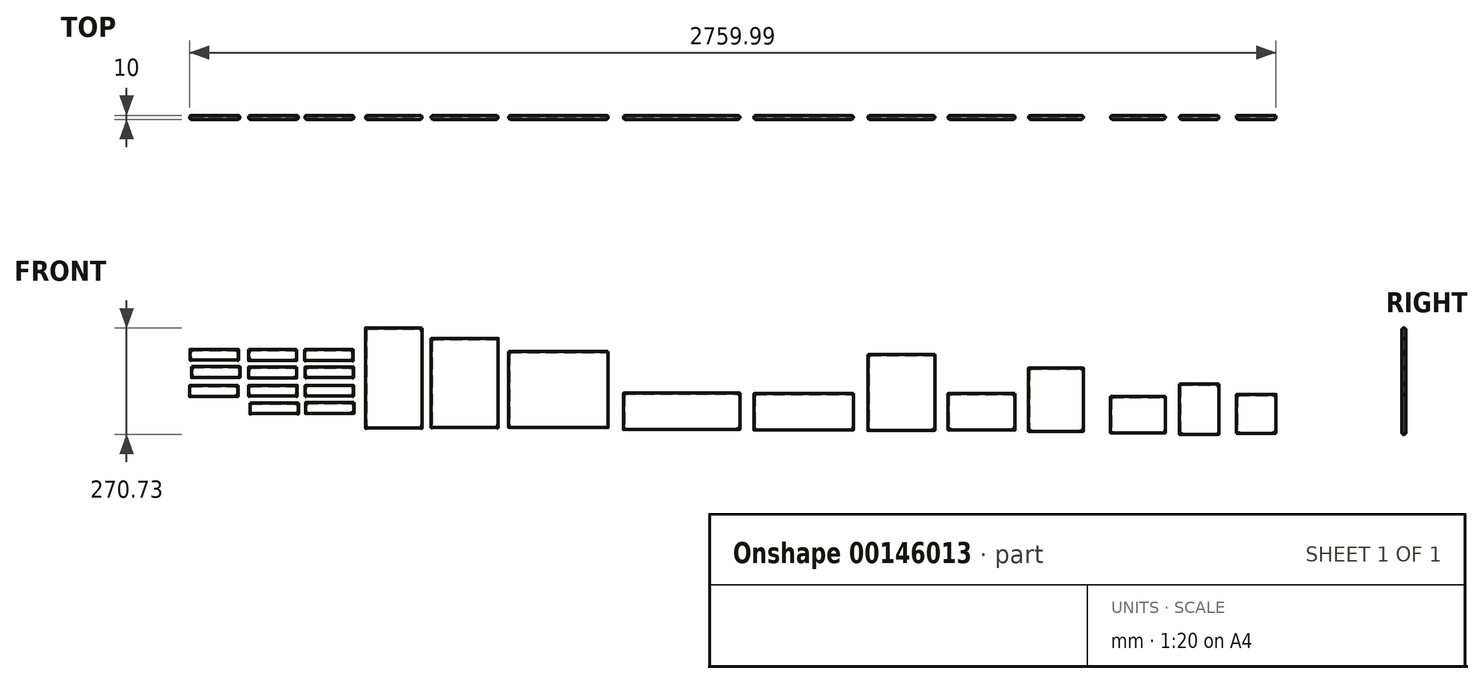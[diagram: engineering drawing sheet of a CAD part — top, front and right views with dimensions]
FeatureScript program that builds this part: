
annotation { "Feature Type Name" : "Feature", "Feature Type Description" : "" }
export const myFeature = defineFeature(function(context is Context, id is Id, definition is map)
    precondition{}
    {
        {
            var Q0;
            Q0=qCreatedBy(makeId("Front.planeOp"),FACE);
            var sketch = newSketch(context, id + "F0", { "sketchPlane" : qUnion([Q0])});
            skLineSegment(sketch, "E0.bottom", {"start": v(-185.42, 51.02) * mm, "end": v(-62.42, 51.02) * mm});
            skLineSegment(sketch, "E0.top", {"start": v(-185.42, 79.02) * mm, "end": v(-62.42, 79.02) * mm});
            skLineSegment(sketch, "E0.left", {"start": v(-185.42, 51.02) * mm, "end": v(-185.42, 79.02) * mm});
            skLineSegment(sketch, "E0.right", {"start": v(-62.42, 51.02) * mm, "end": v(-62.42, 79.02) * mm});
            skLineSegment(sketch, "E1.bottom", {"start": v(-184.61, -39.22) * mm, "end": v(-61.61, -39.22) * mm});
            skLineSegment(sketch, "E1.top", {"start": v(-184.61, -11.22) * mm, "end": v(-61.61, -11.22) * mm});
            skLineSegment(sketch, "E1.left", {"start": v(-184.61, -39.22) * mm, "end": v(-184.61, -11.22) * mm});
            skLineSegment(sketch, "E1.right", {"start": v(-61.61, -39.22) * mm, "end": v(-61.61, -11.22) * mm});
            skLineSegment(sketch, "E2.bottom", {"start": v(-183.78, -83.5) * mm, "end": v(-60.78, -83.5) * mm});
            skLineSegment(sketch, "E2.top", {"start": v(-183.78, -55.5) * mm, "end": v(-60.78, -55.5) * mm});
            skLineSegment(sketch, "E2.left", {"start": v(-183.78, -83.5) * mm, "end": v(-183.78, -55.5) * mm});
            skLineSegment(sketch, "E2.right", {"start": v(-60.78, -83.5) * mm, "end": v(-60.78, -55.5) * mm});
            skLineSegment(sketch, "E3.bottom", {"start": v(-328.72, 51.62) * mm, "end": v(-205.72, 51.62) * mm});
            skLineSegment(sketch, "E3.top", {"start": v(-328.72, 79.62) * mm, "end": v(-205.72, 79.62) * mm});
            skLineSegment(sketch, "E3.left", {"start": v(-328.72, 51.62) * mm, "end": v(-328.72, 79.62) * mm});
            skLineSegment(sketch, "E3.right", {"start": v(-205.72, 51.62) * mm, "end": v(-205.72, 79.62) * mm});
            skLineSegment(sketch, "E4.bottom", {"start": v(-184.79, 7.45) * mm, "end": v(-61.79, 7.45) * mm});
            skLineSegment(sketch, "E4.top", {"start": v(-184.79, 35.45) * mm, "end": v(-61.79, 35.45) * mm});
            skLineSegment(sketch, "E4.left", {"start": v(-184.79, 7.45) * mm, "end": v(-184.79, 35.45) * mm});
            skLineSegment(sketch, "E4.right", {"start": v(-61.79, 7.45) * mm, "end": v(-61.79, 35.45) * mm});
            skLineSegment(sketch, "E5.bottom", {"start": v(-328.7, 6.95) * mm, "end": v(-205.7, 6.95) * mm});
            skLineSegment(sketch, "E5.top", {"start": v(-328.7, 34.95) * mm, "end": v(-205.7, 34.95) * mm});
            skLineSegment(sketch, "E5.left", {"start": v(-328.7, 6.95) * mm, "end": v(-328.7, 34.95) * mm});
            skLineSegment(sketch, "E5.right", {"start": v(-205.7, 6.95) * mm, "end": v(-205.7, 34.95) * mm});
            skLineSegment(sketch, "E6.bottom", {"start": v(-477.03, 51.95) * mm, "end": v(-354.03, 51.95) * mm});
            skLineSegment(sketch, "E6.top", {"start": v(-477.03, 79.95) * mm, "end": v(-354.03, 79.95) * mm});
            skLineSegment(sketch, "E6.left", {"start": v(-477.03, 51.95) * mm, "end": v(-477.03, 79.95) * mm});
            skLineSegment(sketch, "E6.right", {"start": v(-354.03, 51.95) * mm, "end": v(-354.03, 79.95) * mm});
            skLineSegment(sketch, "E7.bottom", {"start": v(-473.24, 7.86) * mm, "end": v(-350.24, 7.86) * mm});
            skLineSegment(sketch, "E7.top", {"start": v(-473.24, 35.86) * mm, "end": v(-350.24, 35.86) * mm});
            skLineSegment(sketch, "E7.left", {"start": v(-473.24, 7.86) * mm, "end": v(-473.24, 35.86) * mm});
            skLineSegment(sketch, "E7.right", {"start": v(-350.24, 7.86) * mm, "end": v(-350.24, 35.86) * mm});
            skLineSegment(sketch, "E8.bottom", {"start": v(-478.2, -39.92) * mm, "end": v(-355.2, -39.92) * mm});
            skLineSegment(sketch, "E8.top", {"start": v(-478.2, -11.92) * mm, "end": v(-355.2, -11.92) * mm});
            skLineSegment(sketch, "E8.left", {"start": v(-478.2, -39.92) * mm, "end": v(-478.2, -11.92) * mm});
            skLineSegment(sketch, "E8.right", {"start": v(-355.2, -39.92) * mm, "end": v(-355.2, -11.92) * mm});
            skLineSegment(sketch, "E9.bottom", {"start": v(-324.63, -84.24) * mm, "end": v(-201.63, -84.24) * mm});
            skLineSegment(sketch, "E9.top", {"start": v(-324.63, -56.24) * mm, "end": v(-201.63, -56.24) * mm});
            skLineSegment(sketch, "E9.left", {"start": v(-324.63, -84.24) * mm, "end": v(-324.63, -56.24) * mm});
            skLineSegment(sketch, "E9.right", {"start": v(-201.63, -84.24) * mm, "end": v(-201.63, -56.24) * mm});
            skLineSegment(sketch, "E10.bottom", {"start": v(-327.71, -39.33) * mm, "end": v(-204.71, -39.33) * mm});
            skLineSegment(sketch, "E10.top", {"start": v(-327.71, -11.33) * mm, "end": v(-204.71, -11.33) * mm});
            skLineSegment(sketch, "E10.left", {"start": v(-327.71, -39.33) * mm, "end": v(-327.71, -11.33) * mm});
            skLineSegment(sketch, "E10.right", {"start": v(-204.71, -39.33) * mm, "end": v(-204.71, -11.33) * mm});
            skSolve(sketch);
        }
        {
            var Q0;
            Q0 = qSketchRegion(id + "F0", true);
            extrude(context, id + "F1", {"entities" : qUnion([Q0]), "depth" : 10 * mm});
        }
        {
            var Q0;
            Q0=makeQuery(id+"F1.opExtrude","SWEPT_FACE",FACE,{"disambiguationData":[OSD([sQuery(id+"F0.wireOp",EDGE,"E0.bottom")])]});
            var Q1;
            Q1=makeQuery(id+"F1.opExtrude","SWEPT_FACE",FACE,{"disambiguationData":[OSD([sQuery(id+"F0.wireOp",EDGE,"E4.bottom")])]});
            var Q2;
            Q2=makeQuery(id+"F1.opExtrude","SWEPT_FACE",FACE,{"disambiguationData":[OSD([sQuery(id+"F0.wireOp",EDGE,"E7.bottom")])]});
            var Q3;
            Q3=makeQuery(id+"F1.opExtrude","SWEPT_FACE",FACE,{"disambiguationData":[OSD([sQuery(id+"F0.wireOp",EDGE,"E3.bottom")])]});
            var Q4;
            Q4=makeQuery(id+"F1.opExtrude","SWEPT_FACE",FACE,{"disambiguationData":[OSD([sQuery(id+"F0.wireOp",EDGE,"E6.bottom")])]});
            var Q5;
            Q5=makeQuery(id+"F1.opExtrude","SWEPT_FACE",FACE,{"disambiguationData":[OSD([sQuery(id+"F0.wireOp",EDGE,"E8.bottom")])]});
            var Q6;
            Q6=makeQuery(id+"F1.opExtrude","SWEPT_FACE",FACE,{"disambiguationData":[OSD([sQuery(id+"F0.wireOp",EDGE,"E9.bottom")])]});
            var Q7;
            Q7=makeQuery(id+"F1.opExtrude","SWEPT_FACE",FACE,{"disambiguationData":[OSD([sQuery(id+"F0.wireOp",EDGE,"E10.bottom")])]});
            var Q8;
            Q8=makeQuery(id+"F1.opExtrude","SWEPT_FACE",FACE,{"disambiguationData":[OSD([sQuery(id+"F0.wireOp",EDGE,"E5.bottom")])]});
            var Q9;
            Q9=makeQuery(id+"F1.opExtrude","SWEPT_FACE",FACE,{"disambiguationData":[OSD([sQuery(id+"F0.wireOp",EDGE,"E2.bottom")])]});
            var Q10;
            Q10=makeQuery(id+"F1.opExtrude","SWEPT_FACE",FACE,{"disambiguationData":[OSD([sQuery(id+"F0.wireOp",EDGE,"E1.bottom")])]});
            shell(context, id + "F2", {"entities" : qUnion([Q0, Q1, Q2, Q3, Q4, Q5, Q6, Q7, Q8, Q9, Q10]), "thickness" : 2.5 * mm});
        }
        {
            var Q0;
            Q0=qCreatedBy(makeId("Front.planeOp"),FACE);
            var sketch = newSketch(context, id + "F3", { "sketchPlane" : qUnion([Q0])});
            skLineSegment(sketch, "E11.bottom", {"start": v(-31.23, 134.3) * mm, "end": v(112.77, 134.3) * mm});
            skLineSegment(sketch, "E11.top", {"start": v(-31.23, -120.7) * mm, "end": v(112.77, -120.7) * mm});
            skLineSegment(sketch, "E11.left", {"start": v(-31.23, 134.3) * mm, "end": v(-31.23, -120.7) * mm});
            skLineSegment(sketch, "E11.right", {"start": v(112.77, 134.3) * mm, "end": v(112.77, -120.7) * mm});
            skLineSegment(sketch, "E12.bottom", {"start": v(135.53, 107.6) * mm, "end": v(305.53, 107.6) * mm});
            skLineSegment(sketch, "E12.top", {"start": v(135.53, -119.4) * mm, "end": v(305.53, -119.4) * mm});
            skLineSegment(sketch, "E12.left", {"start": v(135.53, 107.6) * mm, "end": v(135.53, -119.4) * mm});
            skLineSegment(sketch, "E12.right", {"start": v(305.53, 107.6) * mm, "end": v(305.53, -119.4) * mm});
            skLineSegment(sketch, "E13.bottom", {"start": v(332.44, 73.9) * mm, "end": v(585.44, 73.9) * mm});
            skLineSegment(sketch, "E13.top", {"start": v(332.44, -119.1) * mm, "end": v(585.44, -119.1) * mm});
            skLineSegment(sketch, "E13.left", {"start": v(332.44, 73.9) * mm, "end": v(332.44, -119.1) * mm});
            skLineSegment(sketch, "E13.right", {"start": v(585.44, 73.9) * mm, "end": v(585.44, -119.1) * mm});
            skLineSegment(sketch, "E14.bottom", {"start": v(623.81, -30.97) * mm, "end": v(919.81, -30.97) * mm});
            skLineSegment(sketch, "E14.top", {"start": v(623.81, -123.97) * mm, "end": v(919.81, -123.97) * mm});
            skLineSegment(sketch, "E14.left", {"start": v(623.81, -30.97) * mm, "end": v(623.81, -123.97) * mm});
            skLineSegment(sketch, "E14.right", {"start": v(919.81, -30.97) * mm, "end": v(919.81, -123.97) * mm});
            skLineSegment(sketch, "E15.bottom", {"start": v(955.2, -32.5) * mm, "end": v(1208.2, -32.5) * mm});
            skLineSegment(sketch, "E15.top", {"start": v(955.2, -125.5) * mm, "end": v(1208.2, -125.5) * mm});
            skLineSegment(sketch, "E15.left", {"start": v(955.2, -32.5) * mm, "end": v(955.2, -125.5) * mm});
            skLineSegment(sketch, "E15.right", {"start": v(1208.2, -32.5) * mm, "end": v(1208.2, -125.5) * mm});
            skLineSegment(sketch, "E16.bottom", {"start": v(1245.22, 66.68) * mm, "end": v(1415.22, 66.68) * mm});
            skLineSegment(sketch, "E16.top", {"start": v(1245.22, -126.32) * mm, "end": v(1415.22, -126.32) * mm});
            skLineSegment(sketch, "E16.left", {"start": v(1245.22, 66.68) * mm, "end": v(1245.22, -126.32) * mm});
            skLineSegment(sketch, "E16.right", {"start": v(1415.22, 66.68) * mm, "end": v(1415.22, -126.32) * mm});
            skLineSegment(sketch, "E17.bottom", {"start": v(1448.93, -32.02) * mm, "end": v(1618.93, -32.02) * mm});
            skLineSegment(sketch, "E17.top", {"start": v(1448.93, -125.02) * mm, "end": v(1618.93, -125.02) * mm});
            skLineSegment(sketch, "E17.left", {"start": v(1448.93, -32.02) * mm, "end": v(1448.93, -125.02) * mm});
            skLineSegment(sketch, "E17.right", {"start": v(1618.93, -32.02) * mm, "end": v(1618.93, -125.02) * mm});
            skLineSegment(sketch, "E18.bottom", {"start": v(1653.54, 32.98) * mm, "end": v(1792.54, 32.98) * mm});
            skLineSegment(sketch, "E18.top", {"start": v(1653.54, -129.02) * mm, "end": v(1792.54, -129.02) * mm});
            skLineSegment(sketch, "E18.left", {"start": v(1653.54, 32.98) * mm, "end": v(1653.54, -129.02) * mm});
            skLineSegment(sketch, "E18.right", {"start": v(1792.54, 32.98) * mm, "end": v(1792.54, -129.02) * mm});
            skLineSegment(sketch, "E19.bottom", {"start": v(1861.67, -40.12) * mm, "end": v(2000.67, -40.12) * mm});
            skLineSegment(sketch, "E19.top", {"start": v(1861.67, -133.12) * mm, "end": v(2000.67, -133.12) * mm});
            skLineSegment(sketch, "E19.left", {"start": v(1861.67, -40.12) * mm, "end": v(1861.67, -133.12) * mm});
            skLineSegment(sketch, "E19.right", {"start": v(2000.67, -40.12) * mm, "end": v(2000.67, -133.12) * mm});
            skLineSegment(sketch, "E20.bottom", {"start": v(2036.78, -8.43) * mm, "end": v(2136.78, -8.43) * mm});
            skLineSegment(sketch, "E20.top", {"start": v(2036.78, -136.43) * mm, "end": v(2136.78, -136.43) * mm});
            skLineSegment(sketch, "E20.left", {"start": v(2036.78, -8.43) * mm, "end": v(2036.78, -136.43) * mm});
            skLineSegment(sketch, "E20.right", {"start": v(2136.78, -8.43) * mm, "end": v(2136.78, -136.43) * mm});
            skLineSegment(sketch, "E21.bottom", {"start": v(2181.78, -34.27) * mm, "end": v(2281.78, -34.27) * mm});
            skLineSegment(sketch, "E21.top", {"start": v(2181.78, -134.27) * mm, "end": v(2281.78, -134.27) * mm});
            skLineSegment(sketch, "E21.left", {"start": v(2181.78, -34.27) * mm, "end": v(2181.78, -134.27) * mm});
            skLineSegment(sketch, "E21.right", {"start": v(2281.78, -34.27) * mm, "end": v(2281.78, -134.27) * mm});
            skSolve(sketch);
        }
        {
            var Q0;
            Q0 = qSketchRegion(id + "F3", true);
            extrude(context, id + "F4", {"entities" : qUnion([Q0]), "depth" : 10 * mm});
        }
        {
            var Q0;
            Q0=makeQuery(id+"F4.opExtrude","SWEPT_FACE",FACE,{"disambiguationData":[OSD([sQuery(id+"F3.wireOp",EDGE,"E11.top")])]});
            var Q1;
            Q1=makeQuery(id+"F4.opExtrude","SWEPT_FACE",FACE,{"disambiguationData":[OSD([sQuery(id+"F3.wireOp",EDGE,"E12.top")])]});
            var Q2;
            Q2=makeQuery(id+"F4.opExtrude","SWEPT_FACE",FACE,{"disambiguationData":[OSD([sQuery(id+"F3.wireOp",EDGE,"E13.top")])]});
            var Q3;
            Q3=makeQuery(id+"F4.opExtrude","SWEPT_FACE",FACE,{"disambiguationData":[OSD([sQuery(id+"F3.wireOp",EDGE,"E14.top")])]});
            var Q4;
            Q4=makeQuery(id+"F4.opExtrude","SWEPT_FACE",FACE,{"disambiguationData":[OSD([sQuery(id+"F3.wireOp",EDGE,"E15.top")])]});
            var Q5;
            Q5=makeQuery(id+"F4.opExtrude","SWEPT_FACE",FACE,{"disambiguationData":[OSD([sQuery(id+"F3.wireOp",EDGE,"E16.top")])]});
            var Q6;
            Q6=makeQuery(id+"F4.opExtrude","SWEPT_FACE",FACE,{"disambiguationData":[OSD([sQuery(id+"F3.wireOp",EDGE,"E17.top")])]});
            var Q7;
            Q7=makeQuery(id+"F4.opExtrude","SWEPT_FACE",FACE,{"disambiguationData":[OSD([sQuery(id+"F3.wireOp",EDGE,"E18.top")])]});
            var Q8;
            Q8=makeQuery(id+"F4.opExtrude","SWEPT_FACE",FACE,{"disambiguationData":[OSD([sQuery(id+"F3.wireOp",EDGE,"E19.top")])]});
            var Q9;
            Q9=makeQuery(id+"F4.opExtrude","SWEPT_FACE",FACE,{"disambiguationData":[OSD([sQuery(id+"F3.wireOp",EDGE,"E20.top")])]});
            var Q10;
            Q10=makeQuery(id+"F4.opExtrude","SWEPT_FACE",FACE,{"disambiguationData":[OSD([sQuery(id+"F3.wireOp",EDGE,"E21.top")])]});
            shell(context, id + "F5", {"entities" : qUnion([Q0, Q1, Q2, Q3, Q4, Q5, Q6, Q7, Q8, Q9, Q10]), "thickness" : 2.5 * mm});
        }
        {
            var Q0;
            Q0=makeQuery(id+"F4.opExtrude","CAP_FACE",FACE,{"disambiguationData":[OSD([sQuery(id+"F3.wireOp",EDGE,"E11.bottom"),sQuery(id+"F3.wireOp",EDGE,"E11.top"),sQuery(id+"F3.wireOp",EDGE,"E11.left"),sQuery(id+"F3.wireOp",EDGE,"E11.right")])],"isStart":false});
            var Q1;
            Q1=makeQuery(id+"F4.opExtrude","CAP_FACE",FACE,{"disambiguationData":[OSD([sQuery(id+"F3.wireOp",EDGE,"E12.bottom"),sQuery(id+"F3.wireOp",EDGE,"E12.top"),sQuery(id+"F3.wireOp",EDGE,"E12.left"),sQuery(id+"F3.wireOp",EDGE,"E12.right")])],"isStart":false});
            var Q2;
            Q2=makeQuery(id+"F4.opExtrude","CAP_FACE",FACE,{"disambiguationData":[OSD([sQuery(id+"F3.wireOp",EDGE,"E13.bottom"),sQuery(id+"F3.wireOp",EDGE,"E13.top"),sQuery(id+"F3.wireOp",EDGE,"E13.left"),sQuery(id+"F3.wireOp",EDGE,"E13.right")])],"isStart":false});
            var Q3;
            Q3=makeQuery(id+"F4.opExtrude","CAP_FACE",FACE,{"disambiguationData":[OSD([sQuery(id+"F3.wireOp",EDGE,"E14.bottom"),sQuery(id+"F3.wireOp",EDGE,"E14.top"),sQuery(id+"F3.wireOp",EDGE,"E14.left"),sQuery(id+"F3.wireOp",EDGE,"E14.right")])],"isStart":false});
            var Q4;
            Q4=makeQuery(id+"F4.opExtrude","CAP_FACE",FACE,{"disambiguationData":[OSD([sQuery(id+"F3.wireOp",EDGE,"E15.bottom"),sQuery(id+"F3.wireOp",EDGE,"E15.top"),sQuery(id+"F3.wireOp",EDGE,"E15.left"),sQuery(id+"F3.wireOp",EDGE,"E15.right")])],"isStart":false});
            var Q5;
            Q5=makeQuery(id+"F4.opExtrude","CAP_FACE",FACE,{"disambiguationData":[OSD([sQuery(id+"F3.wireOp",EDGE,"E16.bottom"),sQuery(id+"F3.wireOp",EDGE,"E16.top"),sQuery(id+"F3.wireOp",EDGE,"E16.left"),sQuery(id+"F3.wireOp",EDGE,"E16.right")])],"isStart":false});
            var Q6;
            Q6=makeQuery(id+"F4.opExtrude","CAP_FACE",FACE,{"disambiguationData":[OSD([sQuery(id+"F3.wireOp",EDGE,"E17.bottom"),sQuery(id+"F3.wireOp",EDGE,"E17.top"),sQuery(id+"F3.wireOp",EDGE,"E17.left"),sQuery(id+"F3.wireOp",EDGE,"E17.right")])],"isStart":false});
            var Q7;
            Q7=makeQuery(id+"F4.opExtrude","CAP_FACE",FACE,{"disambiguationData":[OSD([sQuery(id+"F3.wireOp",EDGE,"E18.bottom"),sQuery(id+"F3.wireOp",EDGE,"E18.top"),sQuery(id+"F3.wireOp",EDGE,"E18.left"),sQuery(id+"F3.wireOp",EDGE,"E18.right")])],"isStart":false});
            var Q8;
            Q8=makeQuery(id+"F4.opExtrude","CAP_FACE",FACE,{"disambiguationData":[OSD([sQuery(id+"F3.wireOp",EDGE,"E19.bottom"),sQuery(id+"F3.wireOp",EDGE,"E19.top"),sQuery(id+"F3.wireOp",EDGE,"E19.left"),sQuery(id+"F3.wireOp",EDGE,"E19.right")])],"isStart":false});
            var Q9;
            Q9=makeQuery(id+"F4.opExtrude","CAP_FACE",FACE,{"disambiguationData":[OSD([sQuery(id+"F3.wireOp",EDGE,"E20.bottom"),sQuery(id+"F3.wireOp",EDGE,"E20.top"),sQuery(id+"F3.wireOp",EDGE,"E20.left"),sQuery(id+"F3.wireOp",EDGE,"E20.right")])],"isStart":false});
            var Q10;
            Q10=makeQuery(id+"F4.opExtrude","CAP_FACE",FACE,{"disambiguationData":[OSD([sQuery(id+"F3.wireOp",EDGE,"E21.bottom"),sQuery(id+"F3.wireOp",EDGE,"E21.top"),sQuery(id+"F3.wireOp",EDGE,"E21.left"),sQuery(id+"F3.wireOp",EDGE,"E21.right")])],"isStart":false});
            var Q11;
            Q11=makeQuery(id+"F4.opExtrude","CAP_FACE",FACE,{"disambiguationData":[OSD([sQuery(id+"F3.wireOp",EDGE,"E20.bottom"),sQuery(id+"F3.wireOp",EDGE,"E20.top"),sQuery(id+"F3.wireOp",EDGE,"E20.left"),sQuery(id+"F3.wireOp",EDGE,"E20.right")])],"isStart":true});
            var Q12;
            Q12=makeQuery(id+"F4.opExtrude","CAP_FACE",FACE,{"disambiguationData":[OSD([sQuery(id+"F3.wireOp",EDGE,"E19.bottom"),sQuery(id+"F3.wireOp",EDGE,"E19.top"),sQuery(id+"F3.wireOp",EDGE,"E19.left"),sQuery(id+"F3.wireOp",EDGE,"E19.right")])],"isStart":true});
            var Q13;
            Q13=makeQuery(id+"F4.opExtrude","CAP_FACE",FACE,{"disambiguationData":[OSD([sQuery(id+"F3.wireOp",EDGE,"E18.bottom"),sQuery(id+"F3.wireOp",EDGE,"E18.top"),sQuery(id+"F3.wireOp",EDGE,"E18.left"),sQuery(id+"F3.wireOp",EDGE,"E18.right")])],"isStart":true});
            var Q14;
            Q14=makeQuery(id+"F4.opExtrude","CAP_FACE",FACE,{"disambiguationData":[OSD([sQuery(id+"F3.wireOp",EDGE,"E17.bottom"),sQuery(id+"F3.wireOp",EDGE,"E17.top"),sQuery(id+"F3.wireOp",EDGE,"E17.left"),sQuery(id+"F3.wireOp",EDGE,"E17.right")])],"isStart":true});
            var Q15;
            Q15=makeQuery(id+"F4.opExtrude","CAP_FACE",FACE,{"disambiguationData":[OSD([sQuery(id+"F3.wireOp",EDGE,"E16.bottom"),sQuery(id+"F3.wireOp",EDGE,"E16.top"),sQuery(id+"F3.wireOp",EDGE,"E16.left"),sQuery(id+"F3.wireOp",EDGE,"E16.right")])],"isStart":true});
            var Q16;
            Q16=makeQuery(id+"F4.opExtrude","CAP_FACE",FACE,{"disambiguationData":[OSD([sQuery(id+"F3.wireOp",EDGE,"E15.bottom"),sQuery(id+"F3.wireOp",EDGE,"E15.top"),sQuery(id+"F3.wireOp",EDGE,"E15.left"),sQuery(id+"F3.wireOp",EDGE,"E15.right")])],"isStart":true});
            var Q17;
            Q17=makeQuery(id+"F4.opExtrude","CAP_FACE",FACE,{"disambiguationData":[OSD([sQuery(id+"F3.wireOp",EDGE,"E14.bottom"),sQuery(id+"F3.wireOp",EDGE,"E14.top"),sQuery(id+"F3.wireOp",EDGE,"E14.left"),sQuery(id+"F3.wireOp",EDGE,"E14.right")])],"isStart":true});
            var Q18;
            Q18=makeQuery(id+"F4.opExtrude","CAP_FACE",FACE,{"disambiguationData":[OSD([sQuery(id+"F3.wireOp",EDGE,"E13.bottom"),sQuery(id+"F3.wireOp",EDGE,"E13.top"),sQuery(id+"F3.wireOp",EDGE,"E13.left"),sQuery(id+"F3.wireOp",EDGE,"E13.right")])],"isStart":true});
            var Q19;
            Q19=makeQuery(id+"F4.opExtrude","CAP_FACE",FACE,{"disambiguationData":[OSD([sQuery(id+"F3.wireOp",EDGE,"E12.bottom"),sQuery(id+"F3.wireOp",EDGE,"E12.top"),sQuery(id+"F3.wireOp",EDGE,"E12.left"),sQuery(id+"F3.wireOp",EDGE,"E12.right")])],"isStart":true});
            var Q20;
            Q20=makeQuery(id+"F4.opExtrude","CAP_FACE",FACE,{"disambiguationData":[OSD([sQuery(id+"F3.wireOp",EDGE,"E11.bottom"),sQuery(id+"F3.wireOp",EDGE,"E11.top"),sQuery(id+"F3.wireOp",EDGE,"E11.left"),sQuery(id+"F3.wireOp",EDGE,"E11.right")])],"isStart":true});
            var Q21;
            Q21=makeQuery(id+"F1.opExtrude","CAP_FACE",FACE,{"disambiguationData":[OSD([sQuery(id+"F0.wireOp",EDGE,"E0.bottom"),sQuery(id+"F0.wireOp",EDGE,"E0.top"),sQuery(id+"F0.wireOp",EDGE,"E0.left"),sQuery(id+"F0.wireOp",EDGE,"E0.right")])],"isStart":false});
            var Q22;
            Q22=makeQuery(id+"F1.opExtrude","CAP_FACE",FACE,{"disambiguationData":[OSD([sQuery(id+"F0.wireOp",EDGE,"E0.bottom"),sQuery(id+"F0.wireOp",EDGE,"E0.top"),sQuery(id+"F0.wireOp",EDGE,"E0.left"),sQuery(id+"F0.wireOp",EDGE,"E0.right")])],"isStart":true});
            var Q23;
            Q23=makeQuery(id+"F1.opExtrude","CAP_FACE",FACE,{"disambiguationData":[OSD([sQuery(id+"F0.wireOp",EDGE,"E4.bottom"),sQuery(id+"F0.wireOp",EDGE,"E4.top"),sQuery(id+"F0.wireOp",EDGE,"E4.left"),sQuery(id+"F0.wireOp",EDGE,"E4.right")])],"isStart":false});
            var Q24;
            Q24=makeQuery(id+"F1.opExtrude","CAP_FACE",FACE,{"disambiguationData":[OSD([sQuery(id+"F0.wireOp",EDGE,"E3.bottom"),sQuery(id+"F0.wireOp",EDGE,"E3.top"),sQuery(id+"F0.wireOp",EDGE,"E3.left"),sQuery(id+"F0.wireOp",EDGE,"E3.right")])],"isStart":false});
            var Q25;
            Q25=makeQuery(id+"F1.opExtrude","CAP_FACE",FACE,{"disambiguationData":[OSD([sQuery(id+"F0.wireOp",EDGE,"E2.bottom"),sQuery(id+"F0.wireOp",EDGE,"E2.top"),sQuery(id+"F0.wireOp",EDGE,"E2.left"),sQuery(id+"F0.wireOp",EDGE,"E2.right")])],"isStart":false});
            var Q26;
            Q26=makeQuery(id+"F1.opExtrude","CAP_FACE",FACE,{"disambiguationData":[OSD([sQuery(id+"F0.wireOp",EDGE,"E1.bottom"),sQuery(id+"F0.wireOp",EDGE,"E1.top"),sQuery(id+"F0.wireOp",EDGE,"E1.left"),sQuery(id+"F0.wireOp",EDGE,"E1.right")])],"isStart":false});
            var Q27;
            Q27=makeQuery(id+"F1.opExtrude","CAP_FACE",FACE,{"disambiguationData":[OSD([sQuery(id+"F0.wireOp",EDGE,"E5.bottom"),sQuery(id+"F0.wireOp",EDGE,"E5.top"),sQuery(id+"F0.wireOp",EDGE,"E5.left"),sQuery(id+"F0.wireOp",EDGE,"E5.right")])],"isStart":false});
            var Q28;
            Q28=makeQuery(id+"F1.opExtrude","CAP_FACE",FACE,{"disambiguationData":[OSD([sQuery(id+"F0.wireOp",EDGE,"E7.bottom"),sQuery(id+"F0.wireOp",EDGE,"E7.top"),sQuery(id+"F0.wireOp",EDGE,"E7.left"),sQuery(id+"F0.wireOp",EDGE,"E7.right")])],"isStart":false});
            var Q29;
            Q29=makeQuery(id+"F1.opExtrude","CAP_FACE",FACE,{"disambiguationData":[OSD([sQuery(id+"F0.wireOp",EDGE,"E6.bottom"),sQuery(id+"F0.wireOp",EDGE,"E6.top"),sQuery(id+"F0.wireOp",EDGE,"E6.left"),sQuery(id+"F0.wireOp",EDGE,"E6.right")])],"isStart":false});
            var Q30;
            Q30=makeQuery(id+"F1.opExtrude","CAP_FACE",FACE,{"disambiguationData":[OSD([sQuery(id+"F0.wireOp",EDGE,"E8.bottom"),sQuery(id+"F0.wireOp",EDGE,"E8.top"),sQuery(id+"F0.wireOp",EDGE,"E8.left"),sQuery(id+"F0.wireOp",EDGE,"E8.right")])],"isStart":false});
            var Q31;
            Q31=makeQuery(id+"F1.opExtrude","CAP_FACE",FACE,{"disambiguationData":[OSD([sQuery(id+"F0.wireOp",EDGE,"E9.bottom"),sQuery(id+"F0.wireOp",EDGE,"E9.top"),sQuery(id+"F0.wireOp",EDGE,"E9.left"),sQuery(id+"F0.wireOp",EDGE,"E9.right")])],"isStart":false});
            var Q32;
            Q32=makeQuery(id+"F1.opExtrude","CAP_FACE",FACE,{"disambiguationData":[OSD([sQuery(id+"F0.wireOp",EDGE,"E10.bottom"),sQuery(id+"F0.wireOp",EDGE,"E10.top"),sQuery(id+"F0.wireOp",EDGE,"E10.left"),sQuery(id+"F0.wireOp",EDGE,"E10.right")])],"isStart":false});
            var Q33;
            Q33=makeQuery(id+"F1.opExtrude","CAP_FACE",FACE,{"disambiguationData":[OSD([sQuery(id+"F0.wireOp",EDGE,"E10.bottom"),sQuery(id+"F0.wireOp",EDGE,"E10.top"),sQuery(id+"F0.wireOp",EDGE,"E10.left"),sQuery(id+"F0.wireOp",EDGE,"E10.right")])],"isStart":true});
            var Q34;
            Q34=makeQuery(id+"F1.opExtrude","CAP_FACE",FACE,{"disambiguationData":[OSD([sQuery(id+"F0.wireOp",EDGE,"E1.bottom"),sQuery(id+"F0.wireOp",EDGE,"E1.top"),sQuery(id+"F0.wireOp",EDGE,"E1.left"),sQuery(id+"F0.wireOp",EDGE,"E1.right")])],"isStart":true});
            var Q35;
            Q35=makeQuery(id+"F1.opExtrude","CAP_FACE",FACE,{"disambiguationData":[OSD([sQuery(id+"F0.wireOp",EDGE,"E5.bottom"),sQuery(id+"F0.wireOp",EDGE,"E5.top"),sQuery(id+"F0.wireOp",EDGE,"E5.left"),sQuery(id+"F0.wireOp",EDGE,"E5.right")])],"isStart":true});
            var Q36;
            Q36=makeQuery(id+"F1.opExtrude","CAP_FACE",FACE,{"disambiguationData":[OSD([sQuery(id+"F0.wireOp",EDGE,"E9.bottom"),sQuery(id+"F0.wireOp",EDGE,"E9.top"),sQuery(id+"F0.wireOp",EDGE,"E9.left"),sQuery(id+"F0.wireOp",EDGE,"E9.right")])],"isStart":true});
            var Q37;
            Q37=makeQuery(id+"F1.opExtrude","CAP_FACE",FACE,{"disambiguationData":[OSD([sQuery(id+"F0.wireOp",EDGE,"E8.bottom"),sQuery(id+"F0.wireOp",EDGE,"E8.top"),sQuery(id+"F0.wireOp",EDGE,"E8.left"),sQuery(id+"F0.wireOp",EDGE,"E8.right")])],"isStart":true});
            var Q38;
            Q38=makeQuery(id+"F1.opExtrude","CAP_FACE",FACE,{"disambiguationData":[OSD([sQuery(id+"F0.wireOp",EDGE,"E2.bottom"),sQuery(id+"F0.wireOp",EDGE,"E2.top"),sQuery(id+"F0.wireOp",EDGE,"E2.left"),sQuery(id+"F0.wireOp",EDGE,"E2.right")])],"isStart":true});
            var Q39;
            Q39=makeQuery(id+"F1.opExtrude","CAP_FACE",FACE,{"disambiguationData":[OSD([sQuery(id+"F0.wireOp",EDGE,"E3.bottom"),sQuery(id+"F0.wireOp",EDGE,"E3.top"),sQuery(id+"F0.wireOp",EDGE,"E3.left"),sQuery(id+"F0.wireOp",EDGE,"E3.right")])],"isStart":true});
            var Q40;
            Q40=makeQuery(id+"F1.opExtrude","CAP_FACE",FACE,{"disambiguationData":[OSD([sQuery(id+"F0.wireOp",EDGE,"E6.bottom"),sQuery(id+"F0.wireOp",EDGE,"E6.top"),sQuery(id+"F0.wireOp",EDGE,"E6.left"),sQuery(id+"F0.wireOp",EDGE,"E6.right")])],"isStart":true});
            var Q41;
            Q41=makeQuery(id+"F1.opExtrude","CAP_FACE",FACE,{"disambiguationData":[OSD([sQuery(id+"F0.wireOp",EDGE,"E4.bottom"),sQuery(id+"F0.wireOp",EDGE,"E4.top"),sQuery(id+"F0.wireOp",EDGE,"E4.left"),sQuery(id+"F0.wireOp",EDGE,"E4.right")])],"isStart":true});
            var Q42;
            Q42=makeQuery(id+"F1.opExtrude","CAP_FACE",FACE,{"disambiguationData":[OSD([sQuery(id+"F0.wireOp",EDGE,"E7.bottom"),sQuery(id+"F0.wireOp",EDGE,"E7.top"),sQuery(id+"F0.wireOp",EDGE,"E7.left"),sQuery(id+"F0.wireOp",EDGE,"E7.right")])],"isStart":true});
            fillet(context, id + "F6", {"entities" : qUnion([Q0, Q1, Q2, Q3, Q4, Q5, Q6, Q7, Q8, Q9, Q10, Q11, Q12, Q13, Q14, Q15, Q16, Q17, Q18, Q19, Q20, Q21, Q22, Q23, Q24, Q25, Q26, Q27, Q28, Q29, Q30, Q31, Q32, Q33, Q34, Q35, Q36, Q37, Q38, Q39, Q40, Q41, Q42]), "radius" : 5 * mm, "tangentPropagation" : true, "allowEdgeOverflow" : false});
        }
    });
